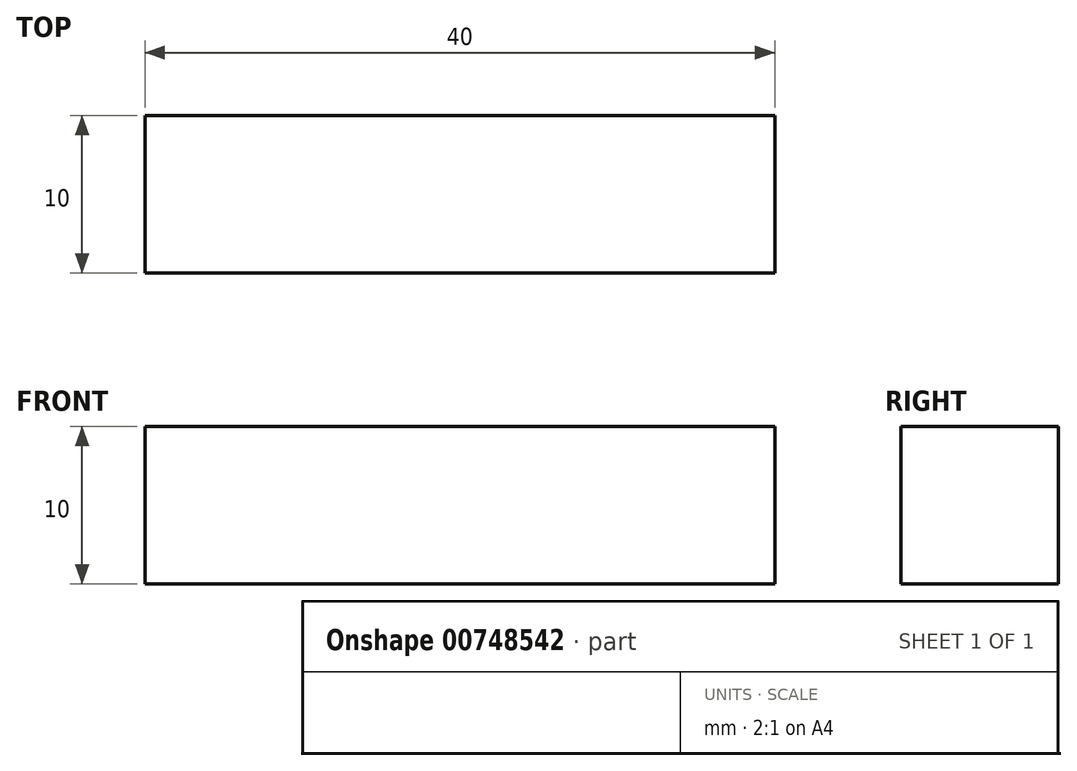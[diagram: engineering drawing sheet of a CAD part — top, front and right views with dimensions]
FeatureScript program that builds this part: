
annotation { "Feature Type Name" : "Feature", "Feature Type Description" : "" }
export const myFeature = defineFeature(function(context is Context, id is Id, definition is map)
    precondition{}
    {
        {
            var Q0;
            Q0=qCreatedBy(makeId("Top.planeOp"),FACE);
            var sketch = newSketch(context, id + "F0", { "sketchPlane" : qUnion([Q0])});
            skLineSegment(sketch, "E0.bottom", {"start": v(-20, 5) * mm, "end": v(20, 5) * mm});
            skLineSegment(sketch, "E0.top", {"start": v(-20, -5) * mm, "end": v(20, -5) * mm});
            skLineSegment(sketch, "E0.left", {"start": v(-20, 5) * mm, "end": v(-20, -5) * mm});
            skLineSegment(sketch, "E0.right", {"start": v(20, 5) * mm, "end": v(20, -5) * mm});
            skPoint(sketch, "E0.middle", {"position": v(0, 0) * mm});
            skSolve(sketch);
        }
        {
            var Q0;
            Q0=makeQuery(id+"F0.imprint","IMPRINT",FACE,{"disambiguationData":[TD([[makeQuery(id+"F0.imprint","IMPRINT",EDGE,{"derivedFrom":sQuery(id+"F0.wireOp",EDGE,"E0.bottom")}),-1.0]])]});
            extrude(context, id + "F1", {"entities" : qUnion([Q0]), "depth" : 10 * mm, "offsetDistance" : 25 * mm});
        }
    });
